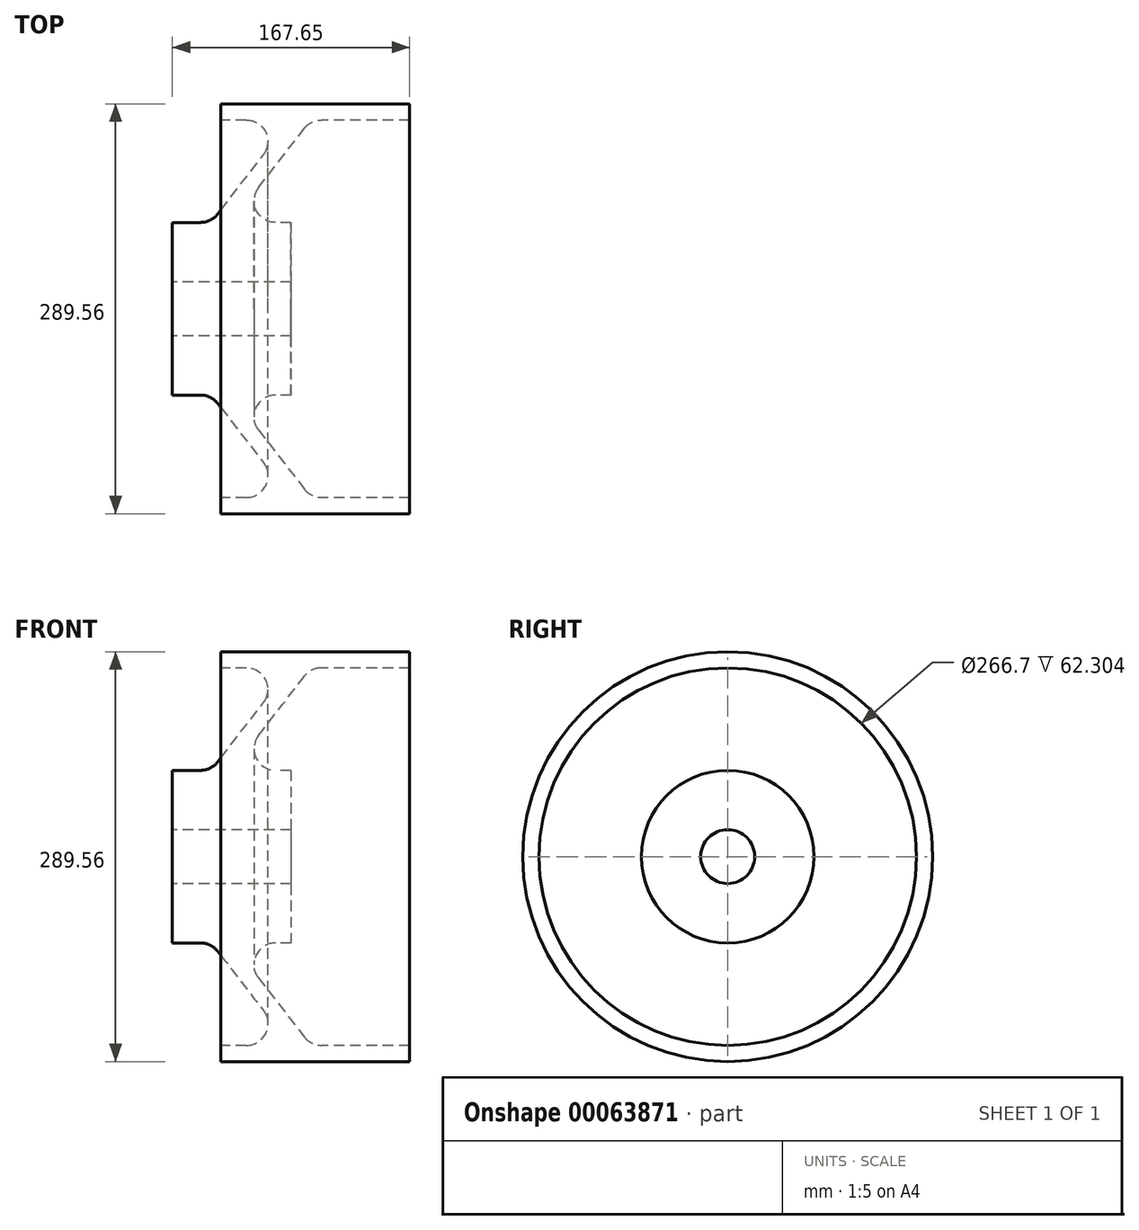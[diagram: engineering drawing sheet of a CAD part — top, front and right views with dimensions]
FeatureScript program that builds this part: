
annotation { "Feature Type Name" : "Feature", "Feature Type Description" : "" }
export const myFeature = defineFeature(function(context is Context, id is Id, definition is map)
    precondition{}
    {
        {
            var Q0;
            Q0=qCreatedBy(makeId("Front.planeOp"),FACE);
            var sketch = newSketch(context, id + "F0", { "sketchPlane" : qUnion([Q0])});
            skLineSegment(sketch, "E0", {"start": v(-194.22, 0) * mm, "end": v(183.85, 0) * mm, "construction": true});
            skLineSegment(sketch, "E1.0", {"start": v(-194.22, 241.3) * mm, "end": v(183.85, 241.3) * mm, "construction": true});
            skLineSegment(sketch, "E2.0", {"start": v(-194.22, 222.25) * mm, "end": v(183.85, 222.25) * mm, "construction": true});
            skLineSegment(sketch, "E3", {"start": v(0, 0) * mm, "end": v(0, 338.49) * mm, "construction": true});
            skLineSegment(sketch, "E4.0", {"start": v(111.13, 0) * mm, "end": v(111.13, 338.49) * mm, "construction": true});
            skLineSegment(sketch, "E5.bottom", {"start": v(111.13, 241.3) * mm, "end": v(-111.12, 241.3) * mm});
            skLineSegment(sketch, "E5.top", {"start": v(111.13, 222.25) * mm, "end": v(-111.12, 222.25) * mm});
            skLineSegment(sketch, "E5.left", {"start": v(111.13, 241.3) * mm, "end": v(111.13, 222.25) * mm});
            skLineSegment(sketch, "E5.right", {"start": v(-111.13, 241.3) * mm, "end": v(-111.13, 222.25) * mm});
            skLineSegment(sketch, "E6.0", {"start": v(-28.58, 0) * mm, "end": v(-28.58, 338.49) * mm, "construction": true});
            skLineSegment(sketch, "E7.0", {"start": v(-168.28, 0) * mm, "end": v(-168.28, 338.49) * mm, "construction": true});
            skLineSegment(sketch, "E8.0", {"start": v(-194.22, 101.6) * mm, "end": v(183.85, 101.6) * mm, "construction": true});
            skLineSegment(sketch, "E9.0", {"start": v(-194.22, 31.75) * mm, "end": v(183.85, 31.75) * mm, "construction": true});
            skLineSegment(sketch, "E10.bottom", {"start": v(-168.28, 101.6) * mm, "end": v(-28.58, 101.6) * mm});
            skLineSegment(sketch, "E10.top", {"start": v(-168.28, 31.75) * mm, "end": v(-28.58, 31.75) * mm});
            skLineSegment(sketch, "E10.left", {"start": v(-168.28, 101.6) * mm, "end": v(-168.28, 31.75) * mm});
            skLineSegment(sketch, "E10.right", {"start": v(-28.58, 101.6) * mm, "end": v(-28.58, 31.75) * mm});
            skLineSegment(sketch, "E11", {"start": v(-98.43, 101.6) * mm, "end": v(-5.19, 222.25) * mm});
            skLineSegment(sketch, "E12.0", {"start": v(-122.5, 101.6) * mm, "end": v(-20.26, 233.9) * mm});
            skSolve(sketch);
        }
        {
            var Q0;
            Q0=qSketchRegion(id+"F0",true);
            var Q1;
            Q1=sQuery(id+"F0.wireOp",EDGE,"E0");
            revolve(context, id + "F1", {"entities" : qUnion([Q0]), "axis" : qUnion([Q1]), "revolveType" : RevolveType.FULL});
        }
        {
            var Q0;
            Q0=makeQuery(id+"F1.opRevolve","SWEPT_FACE",FACE,{"disambiguationData":[OSD([sQuery(id+"F0.wireOp",EDGE,"E11")])]});
            var Q1;
            Q1=makeQuery(id+"F1.opRevolve","SWEPT_FACE",FACE,{"disambiguationData":[OSD([sQuery(id+"F0.wireOp",EDGE,"E12.0")])]});
            fillet(context, id + "F2", {"entities" : qUnion([Q0, Q1]), "radius" : 25.4 * mm, "tangentPropagation" : true, "allowEdgeOverflow" : false});
        }
        {
            var Q0;
            Q0=makeQuery(id+"F1.opRevolve","SWEPT_BODY",BODY,{"disambiguationData":[OSD([sQuery(id+"F0.wireOp",EDGE,"E5.bottom"),sQuery(id+"F0.wireOp",EDGE,"E5.top"),sQuery(id+"F0.wireOp",EDGE,"E5.left"),sQuery(id+"F0.wireOp",EDGE,"E5.right"),sQuery(id+"F0.wireOp",EDGE,"E10.bottom"),sQuery(id+"F0.wireOp",EDGE,"E10.top"),sQuery(id+"F0.wireOp",EDGE,"E10.left"),sQuery(id+"F0.wireOp",EDGE,"E10.right"),sQuery(id+"F0.wireOp",EDGE,"E11"),sQuery(id+"F0.wireOp",EDGE,"E12.0")])]});
            var Q1;
            Q1=qCreatedBy(makeId("Origin.pointOp"),VERTEX);
            transform(context, id + "F3", {"entities" : qUnion([Q0]), "transformType" : TransformType.SCALE_UNIFORMLY, "scale" : .6, "scalePoint" : qUnion([Q1]), "makeCopy" : false});
        }
    });
